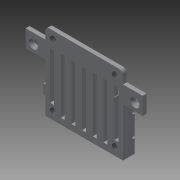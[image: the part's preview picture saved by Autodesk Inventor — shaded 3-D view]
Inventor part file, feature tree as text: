
AUTODESK INVENTOR PART (.ipt)
format: ipt  version: 2015 (Build 190159000, 159)  size: 327,168 bytes
history: native  units: in
note: dims shown in document units (in); Inventor stores cm internally (conversion verified against a paired STEP export)
features: extrude x5, thread x4, sketch x4, projected_geometry x3, reference x2, chamfer x1, fillet x1
ambient origin geometry x8: Origin, YZ Plane, XZ Plane, XY Plane, X Axis, Y Axis, Z Axis, Center Point
bodies: Solid1 (feature_tree)
feature tree (20):
  extrude  "Extrusion1"  Depth=0.1575in TaperAngle=0.0deg
  extrude  "Extrusion2"  Depth=1.5748in
  extrude  "Extrusion3"  Depth=0.2756in
  extrude  "Extrusion4"  Depth=0.3937in
  chamfer  "Chamfer1"  Distance=0.1181in
  thread  "Thread1"  [1 undecoded]
  thread  "Thread2"  [1 undecoded]
  thread  "Thread3"  [1 undecoded]
  thread  "Thread4"  [1 undecoded]
  extrude  "Extrusion5"  Depth=0.0394in
  fillet  "Fillet1"  Radius=0.1969in
  sketch  "Sketch1"  dims[d2=0.0787in d3=0.0in d8=0.1575in d9=0.0in]
  reference  "Reference1"
  sketch  "Sketch2"  dims[d10=1.5748in d11=1.5748in]
  projected_geometry  "Projected Loop1"
  sketch  "Sketch3"  dims[d12=0.1378in d16=0.2756in]
  projected_geometry  "Projected Loop2"
  projected_geometry  "Projected Loop3"
  sketch  "Sketch5"  dims[d18=0.0394in d19=0.3937in d20=0.1181in d21=0.0in d25=0.0787in d26=0.0787in d27=0.0787in d28=0.1969in d29=0.0in d31=0.0394in d32=0.1969in d33=0.0394in d34=0.0787in d35=45.0deg d36=0.3937in d37=0.0in d38=0.3937in d39=0.0in d40=0.3937in d41=0.0in d42=0.3937in d43=0.0in d44=0.315in d45=0.0in d46=1.2598in d47=1.2598in d48=0.2362in d49=0.0787in d51=0.2756in d53=0.1181in d54=1.9685in d56=0.2165in d57=0.3937in d59=0.3937in]
  reference  "Reference2"
note: 4 required parameter values undecoded (feature->parameter linkage not recoverable at this tier; creation-order binding heuristic only, values carry confidence <= 0.55)
